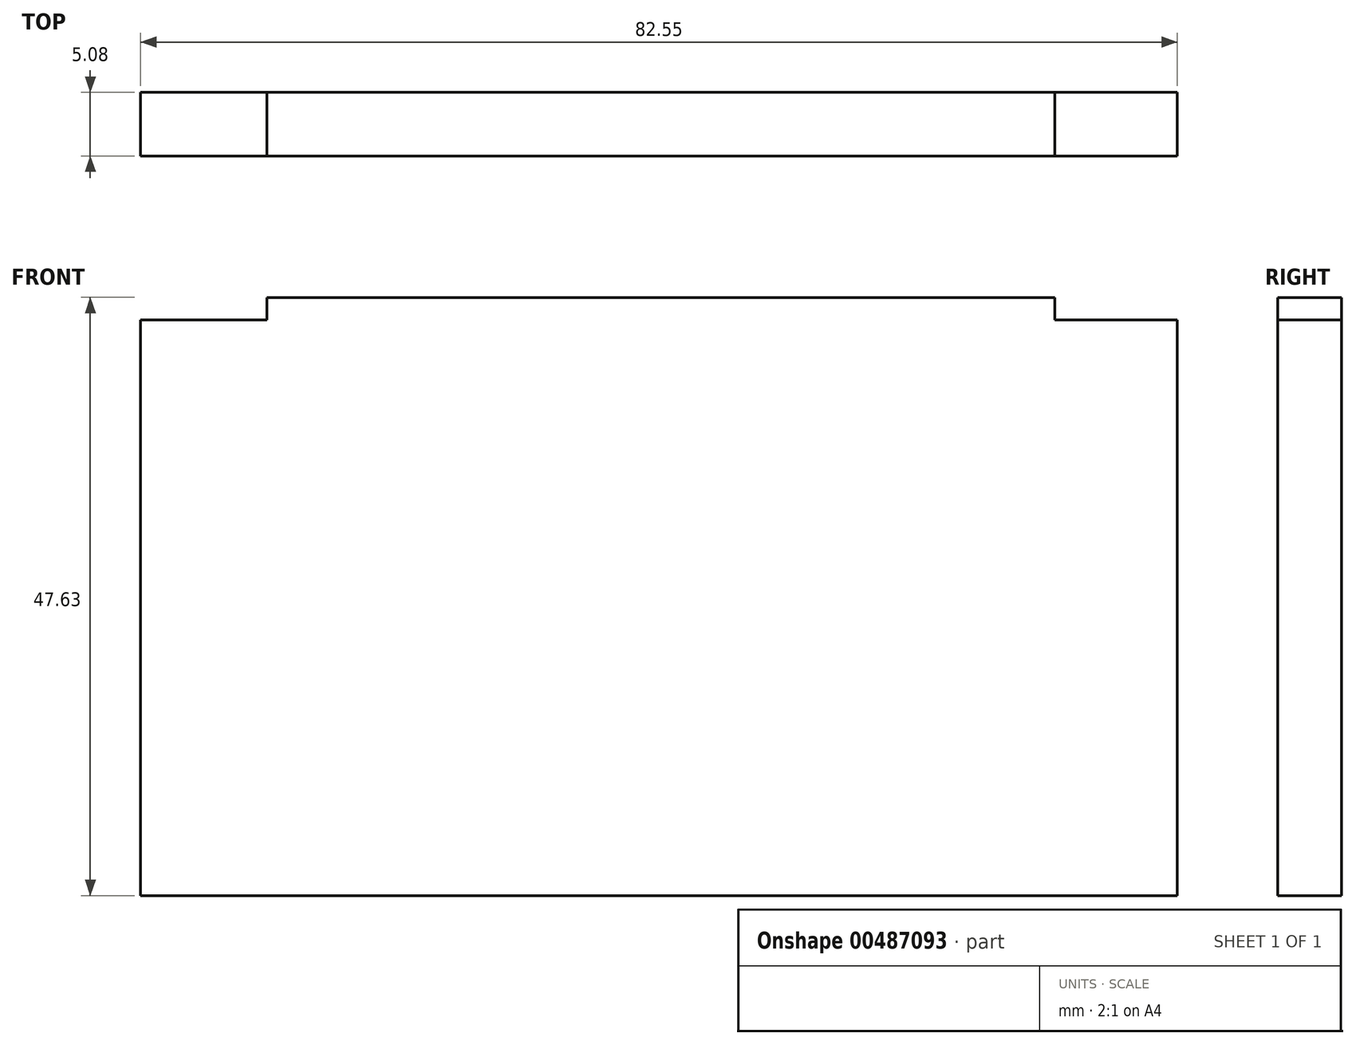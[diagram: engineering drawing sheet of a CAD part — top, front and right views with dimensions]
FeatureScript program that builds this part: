
annotation { "Feature Type Name" : "Feature", "Feature Type Description" : "" }
export const myFeature = defineFeature(function(context is Context, id is Id, definition is map)
    precondition{}
    {
        {
            var Q0;
            Q0=qCreatedBy(makeId("Front.planeOp"),FACE);
            var sketch = newSketch(context, id + "F0", { "sketchPlane" : qUnion([Q0])});
            skLineSegment(sketch, "E0.bottom", {"start": v(-31.37, 22.54) * mm, "end": v(31.37, 22.54) * mm});
            skLineSegment(sketch, "E0.top", {"start": v(-41.43, -25.09) * mm, "end": v(41.12, -25.09) * mm});
            skLineSegment(sketch, "E0.left", {"start": v(-41.43, 20.76) * mm, "end": v(-41.43, -25.09) * mm});
            skLineSegment(sketch, "E0.right", {"start": v(41.12, 20.76) * mm, "end": v(41.12, -25.09) * mm});
            skLineSegment(sketch, "E1.top", {"start": v(41.12, 20.76) * mm, "end": v(31.37, 20.76) * mm});
            skLineSegment(sketch, "E1.right", {"start": v(31.37, 22.54) * mm, "end": v(31.37, 20.76) * mm});
            skLineSegment(sketch, "E2.bottom", {"start": v(-41.43, 20.76) * mm, "end": v(-31.37, 20.76) * mm});
            skLineSegment(sketch, "E2.right", {"start": v(-31.37, 20.76) * mm, "end": v(-31.37, 22.54) * mm});
            skSolve(sketch);
        }
        {
            var Q0;
            Q0=makeQuery(id+"F0.imprint","IMPRINT",FACE,{"disambiguationData":[TD([[makeQuery(id+"F0.imprint","IMPRINT",EDGE,{"derivedFrom":sQuery(id+"F0.wireOp",EDGE,"E0.bottom")}),-1.0]])]});
            var Q1;
            Q1 = qSketchRegion(id + "F0", true);
            extrude(context, id + "F1", {"entities" : qUnion([Q0, Q1]), "endBound" : BoundingType.SYMMETRIC, "depth" : 5.08 * mm});
        }
    });
